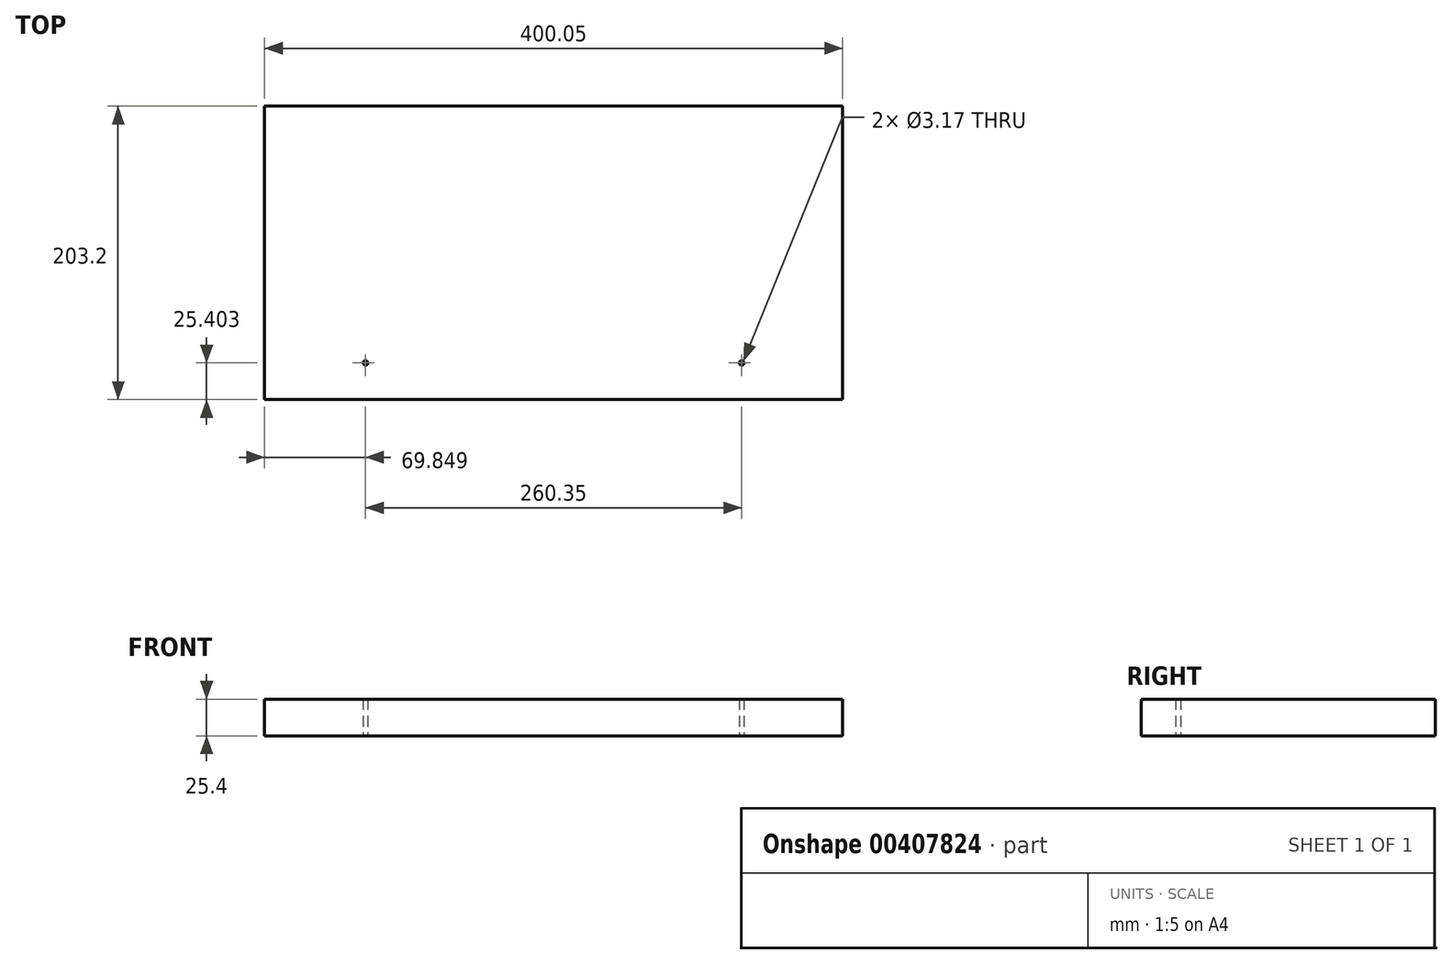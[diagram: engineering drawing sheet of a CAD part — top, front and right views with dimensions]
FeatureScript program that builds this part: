
annotation { "Feature Type Name" : "Feature", "Feature Type Description" : "" }
export const myFeature = defineFeature(function(context is Context, id is Id, definition is map)
    precondition{}
    {
        {
            var Q0;
            Q0=qCreatedBy(makeId("Top.planeOp"),FACE);
            var sketch = newSketch(context, id + "F0", { "sketchPlane" : qUnion([Q0])});
            skLineSegment(sketch, "E0.bottom", {"start": v(-84.47, 107.32) * mm, "end": v(315.58, 107.32) * mm});
            skLineSegment(sketch, "E0.top", {"start": v(-84.47, -95.88) * mm, "end": v(315.58, -95.88) * mm});
            skLineSegment(sketch, "E0.left", {"start": v(-84.47, 107.32) * mm, "end": v(-84.47, -95.88) * mm});
            skLineSegment(sketch, "E0.right", {"start": v(315.58, 107.32) * mm, "end": v(315.58, -95.88) * mm});
            skCircle(sketch, "E1", {"center": v(-14.62, -70.48) * mm, "radius": 1.59 * mm});
            skCircle(sketch, "E2", {"center": v(245.73, -70.48) * mm, "radius": 1.59 * mm});
            skSolve(sketch);
        }
        {
            var Q0;
            Q0=makeQuery(id+"F0.imprint","IMPRINT",FACE,{"disambiguationData":[TD([[makeQuery(id+"F0.imprint","IMPRINT",EDGE,{"derivedFrom":sQuery(id+"F0.wireOp",EDGE,"E0.bottom")}),-1.0]])]});
            extrude(context, id + "F1", {"entities" : qUnion([Q0]), "depth" : 25.4 * mm});
        }
    });
